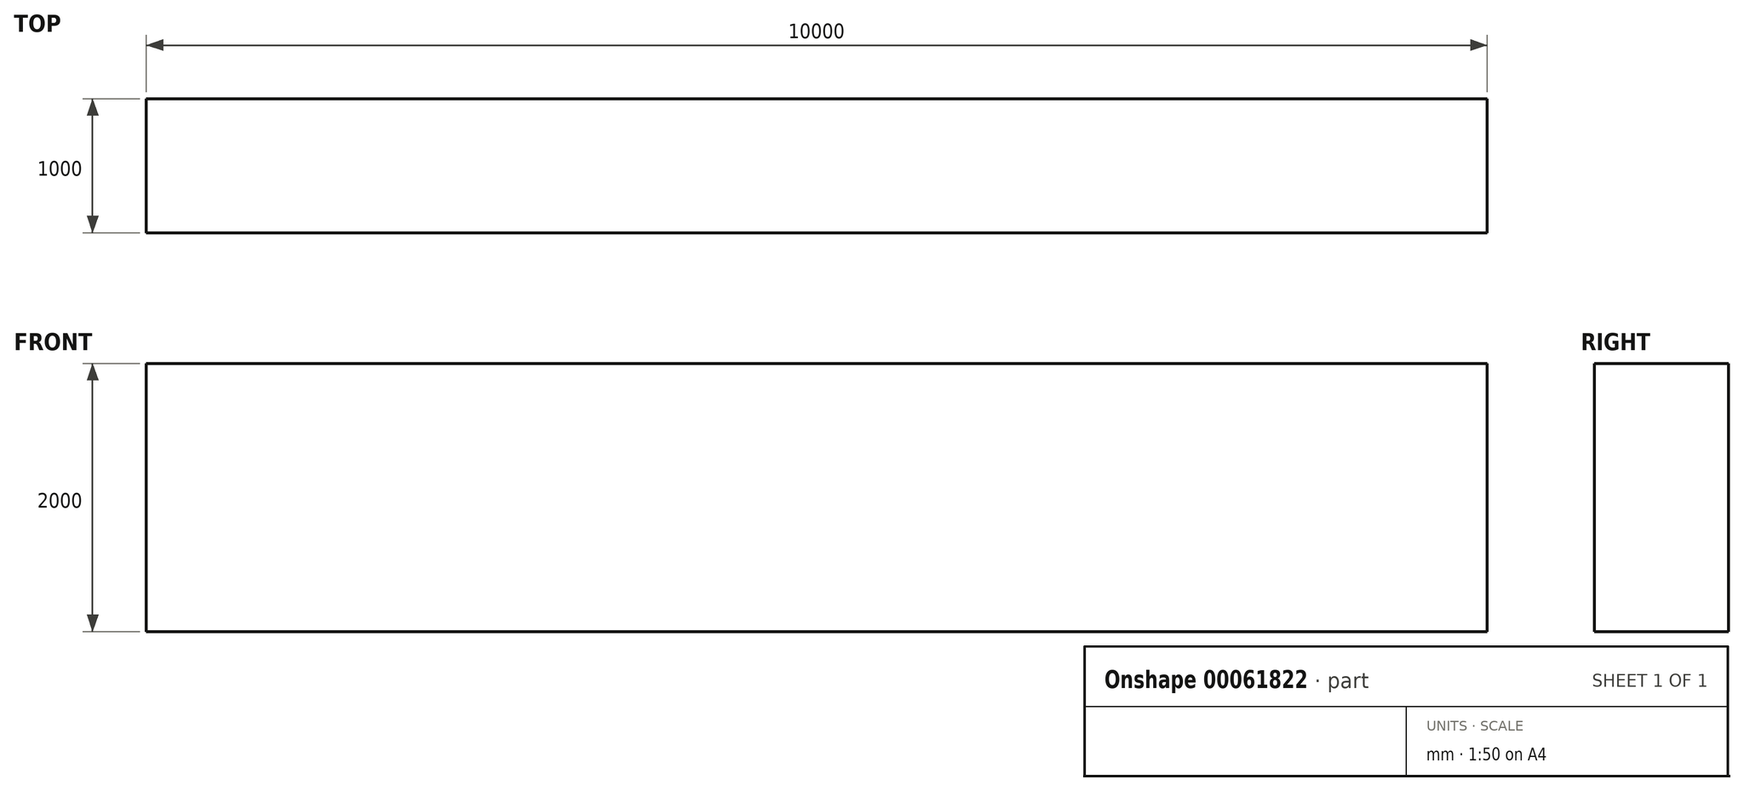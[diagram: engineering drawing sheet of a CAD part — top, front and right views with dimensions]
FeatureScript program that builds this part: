
annotation { "Feature Type Name" : "Feature", "Feature Type Description" : "" }
export const myFeature = defineFeature(function(context is Context, id is Id, definition is map)
    precondition{}
    {
        {
            var Q0;
            Q0=qCreatedBy(makeId("Right.planeOp"),FACE);
            var sketch = newSketch(context, id + "F0", { "sketchPlane" : qUnion([Q0])});
            skLineSegment(sketch, "E0.bottom", {"start": v(500, -1000) * mm, "end": v(-500, -1000) * mm});
            skLineSegment(sketch, "E0.top", {"start": v(500, 1000) * mm, "end": v(-500, 1000) * mm});
            skLineSegment(sketch, "E0.left", {"start": v(500, -1000) * mm, "end": v(500, 1000) * mm});
            skLineSegment(sketch, "E0.right", {"start": v(-500, -1000) * mm, "end": v(-500, 1000) * mm});
            skPoint(sketch, "E0.middle", {"position": v(0, 0) * mm});
            skSolve(sketch);
        }
        {
            var Q0;
            Q0=makeQuery(id+"F0.imprint","IMPRINT",FACE,{"disambiguationData":[TD([[makeQuery(id+"F0.imprint","IMPRINT",EDGE,{"derivedFrom":sQuery(id+"F0.wireOp",EDGE,"E0.bottom")}),-1.0]])]});
            extrude(context, id + "F1", {"entities" : qUnion([Q0]), "depth" : 10000 * mm});
        }
    });
